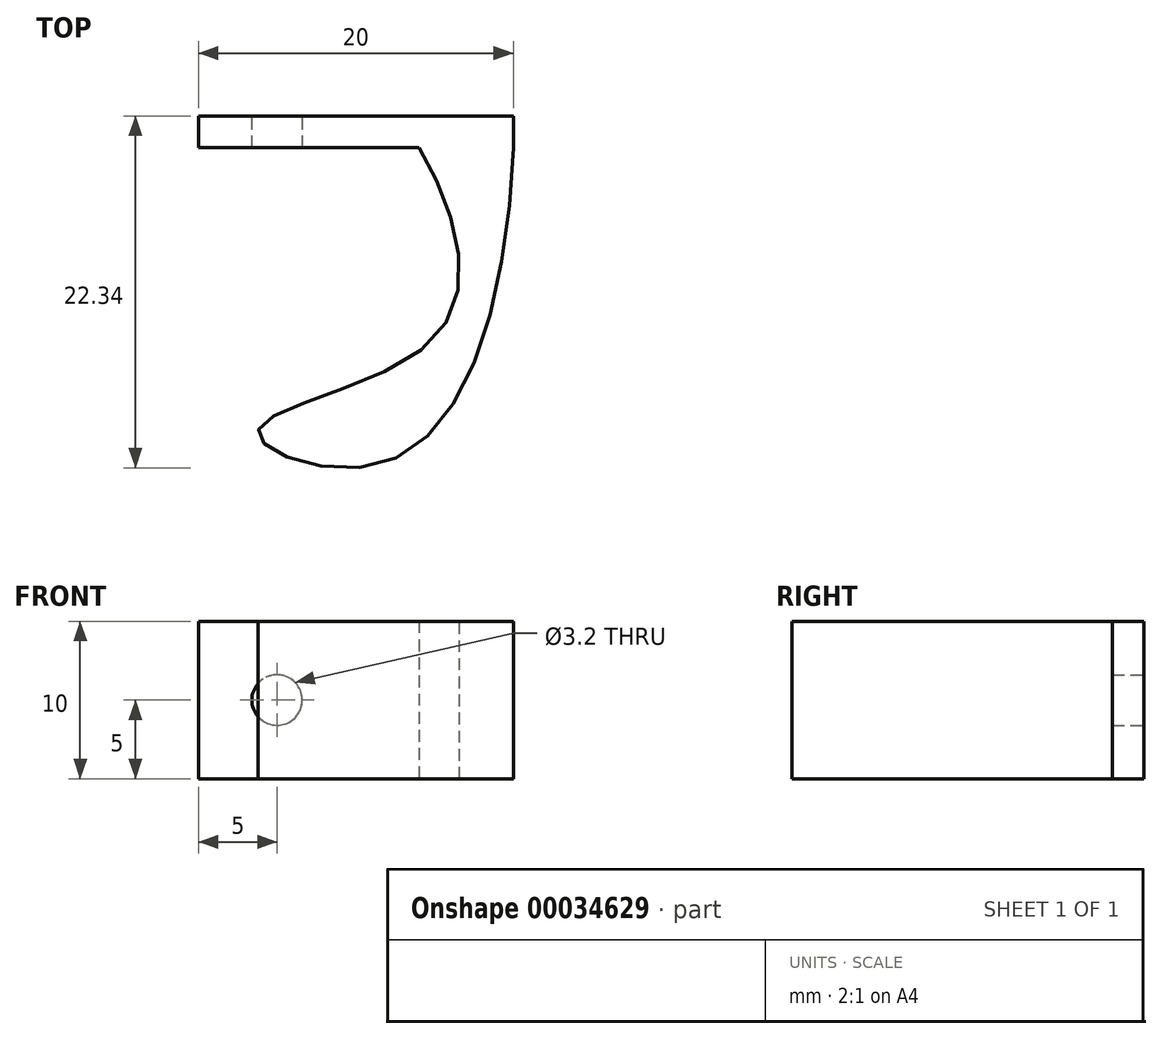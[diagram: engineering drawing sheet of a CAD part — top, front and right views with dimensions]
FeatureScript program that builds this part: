
annotation { "Feature Type Name" : "Feature", "Feature Type Description" : "" }
export const myFeature = defineFeature(function(context is Context, id is Id, definition is map)
    precondition{}
    {
        {
            var Q0;
            Q0=qCreatedBy(makeId("Top.planeOp"),FACE);
            var sketch = newSketch(context, id + "F0", { "sketchPlane" : qUnion([Q0])});
            skLineSegment(sketch, "E0.bottom", {"start": v(0, 0) * mm, "end": v(20, 0) * mm});
            skLineSegment(sketch, "E0.top", {"start": v(0, 2) * mm, "end": v(20, 2) * mm});
            skLineSegment(sketch, "E0.left", {"start": v(0, 0) * mm, "end": v(0, 2) * mm});
            skLineSegment(sketch, "E0.right", {"start": v(20, 0) * mm, "end": v(20, 2) * mm});
            skFitSpline(sketch, "E1", {"points": [v(20, 0) * mm, v(11.8, -20) * mm, v(3.8, -18) * mm, v(15.07, -12) * mm, v(14, 0) * mm], "startDerivative": vector(-3.3, -84.59) * mm, "endDerivative": vector(-27.54, 45) * mm});
            skSolve(sketch);
        }
        {
            var Q0;
            Q0 = qSketchRegion(id + "F0", true);
            var Q1;
            Q1=makeQuery(id+"F0.imprint","IMPRINT",FACE,{"disambiguationData":[TD([[makeQuery(id+"F0.imprint","IMPRINT",EDGE,{"derivedFrom":sQuery(id+"F0.wireOp",EDGE,"E0.top")}),-1.0]])]});
            extrude(context, id + "F1", {"entities" : qUnion([Q0, Q1]), "depth" : 10 * mm});
        }
        {
            var Q0;
            Q0=makeQuery(id+"F1.opExtrude","SWEPT_FACE",FACE,{"disambiguationData":[OSD([sQuery(id+"F0.wireOp",EDGE,"E0.top")])]});
            var sketch = newSketch(context, id + "F2", { "sketchPlane" : qUnion([Q0])});
            skCircle(sketch, "E2", {"center": v(-5, 5) * mm, "radius": 1.6 * mm});
            skSolve(sketch);
        }
        {
            var Q0;
            Q0=makeQuery(id+"F2.imprint","IMPRINT",FACE,{"disambiguationData":[TD([[makeQuery(id+"F2.imprint","IMPRINT",EDGE,{"derivedFrom":sQuery(id+"F2.wireOp",EDGE,"E2")}),1.0]])]});
            extrude(context, id + "F3", {"entities" : qUnion([Q0]), "operationType" : NewBodyOperationType.REMOVE, "endBound" : BoundingType.UP_TO_NEXT, "oppositeDirection" : true, "depth" : 25 * mm});
        }
    });
